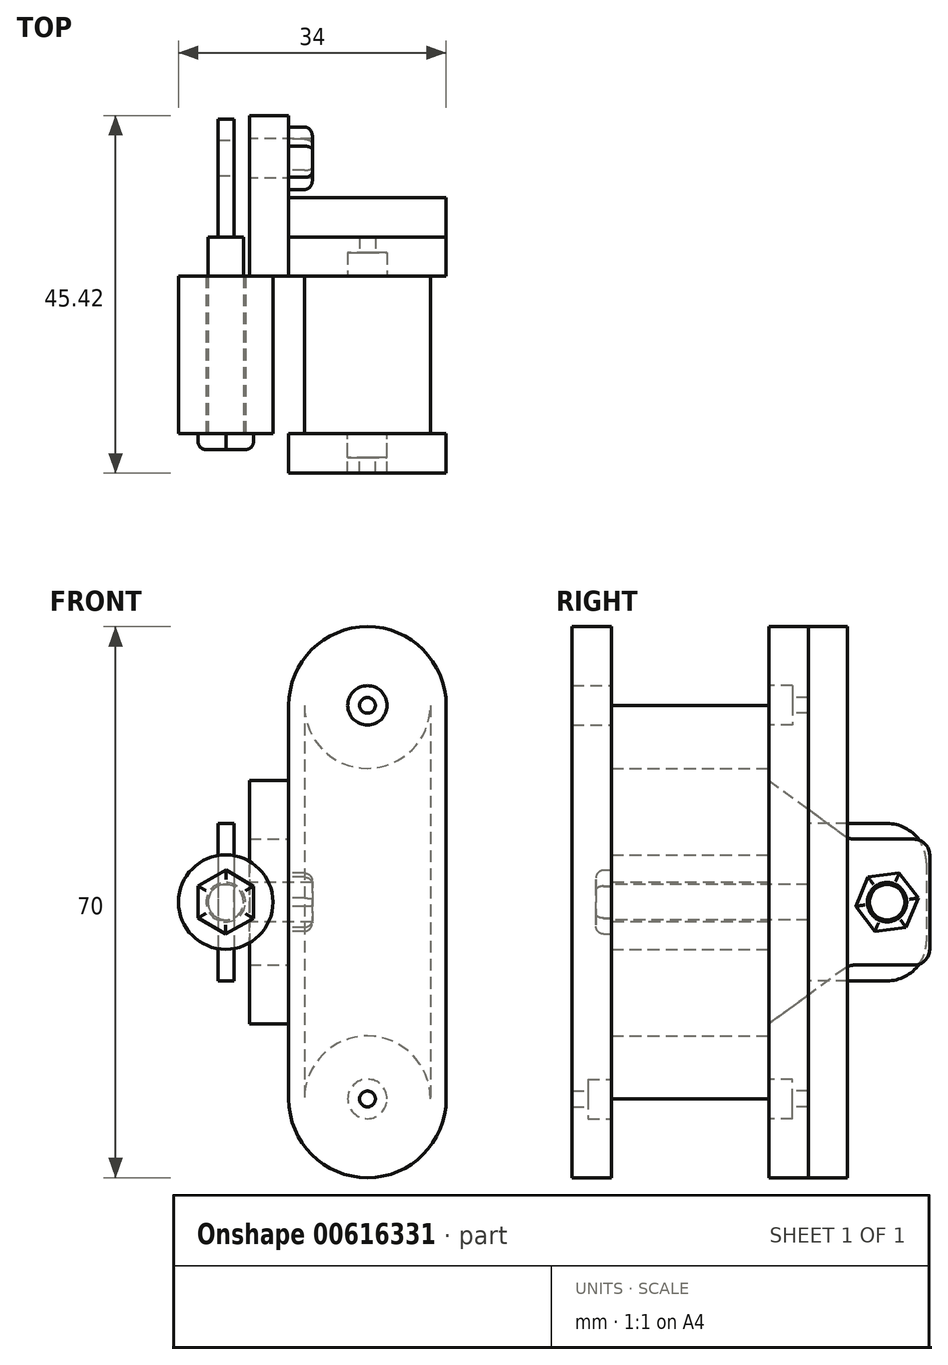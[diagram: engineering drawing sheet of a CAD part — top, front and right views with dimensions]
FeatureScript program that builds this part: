
annotation { "Feature Type Name" : "Feature", "Feature Type Description" : "" }
export const myFeature = defineFeature(function(context is Context, id is Id, definition is map)
    precondition{}
    {
        {
            var Q0;
            Q0=qCreatedBy(makeId("Right.planeOp"),FACE);
            var sketch = newSketch(context, id + "F0", { "sketchPlane" : qUnion([Q0])});
            skLineSegment(sketch, "E0.bottom", {"start": v(10, 0) * mm, "end": v(-10, 0) * mm});
            skLineSegment(sketch, "E0.top", {"start": v(10, -25) * mm, "end": v(-10, -25) * mm});
            skLineSegment(sketch, "E0.left", {"start": v(10, 0) * mm, "end": v(10, -25) * mm});
            skLineSegment(sketch, "E0.right", {"start": v(-10, 0) * mm, "end": v(-10, -25) * mm});
            skPoint(sketch, "E0.middle", {"position": v(0, -12.5) * mm});
            skSolve(sketch);
        }
        {
            var Q0;
            Q0 = qSketchRegion(id + "F0", true);
            extrude(context, id + "F1", {"entities" : qUnion([Q0]), "depth" : 16 * mm, "offsetDistance" : 25 * mm});
        }
        {
            var Q0;
            Q0=makeQuery(id+"F1.opExtrude","SWEPT_FACE",FACE,{"disambiguationData":[OSD([sQuery(id+"F0.wireOp",EDGE,"E0.left")])]});
            var sketch = newSketch(context, id + "F2", { "sketchPlane" : qUnion([Q0])});
            skArc(sketch, "E1", {"start": v(0, -25) * mm, "mid": v(-8, -17) * mm, "end": v(-16, -25) * mm});
            skLineSegment(sketch, "E2", {"start": v(-16, -25) * mm, "end": v(0, -25) * mm});
            skSolve(sketch);
        }
        {
            var Q0;
            Q0 = qSketchRegion(id + "F2", true);
            extrude(context, id + "F3", {"entities" : qUnion([Q0]), "operationType" : NewBodyOperationType.REMOVE, "endBound" : BoundingType.THROUGH_ALL, "oppositeDirection" : true, "depth" : 25 * mm, "offsetDistance" : 25 * mm});
        }
        {
            var Q0;
            Q0=makeQuery(id+"F1.opExtrude","SWEPT_FACE",FACE,{"disambiguationData":[OSD([sQuery(id+"F0.wireOp",EDGE,"E0.left")])]});
            var sketch = newSketch(context, id + "F4", { "sketchPlane" : qUnion([Q0])});
            skArc(sketch, "E3", {"start": v(-18, -25) * mm, "mid": v(-8, -35) * mm, "end": v(2, -25) * mm});
            skLineSegment(sketch, "E4", {"start": v(-18, -25) * mm, "end": v(-18, 0) * mm});
            skLineSegment(sketch, "E5", {"start": v(-18, 0) * mm, "end": v(2, 0) * mm});
            skLineSegment(sketch, "E6", {"start": v(2, 0) * mm, "end": v(2, -25) * mm});
            skSolve(sketch);
        }
        {
            var Q0;
            Q0 = qSketchRegion(id + "F4", true);
            extrude(context, id + "F5", {"entities" : qUnion([Q0]), "operationType" : NewBodyOperationType.ADD, "depth" : 5 * mm, "offsetDistance" : 25 * mm});
        }
        {
            var Q0;
            Q0=makeQuery(id+"F5.opExtrude","CAP_FACE",FACE,{"disambiguationData":[OSD([sQuery(id+"F4.wireOp",EDGE,"E3"),sQuery(id+"F4.wireOp",EDGE,"E4"),sQuery(id+"F4.wireOp",EDGE,"E5"),sQuery(id+"F4.wireOp",EDGE,"E6")])],"isStart":true});
            var sketch = newSketch(context, id + "F6", { "sketchPlane" : qUnion([Q0])});
            skCircle(sketch, "E7", {"center": v(8, -25) * mm, "radius": 2.5 * mm});
            skSolve(sketch);
        }
        {
            var Q0;
            Q0 = qSketchRegion(id + "F6", true);
            extrude(context, id + "F7", {"entities" : qUnion([Q0]), "operationType" : NewBodyOperationType.REMOVE, "oppositeDirection" : true, "depth" : 3 * mm, "offsetDistance" : 25 * mm});
        }
        {
            var Q0;
            Q0=makeQuery(id+"F7.boolean.opBoolean","COPY",FACE,{"derivedFrom":makeQuery(id+"F7.opExtrude","CAP_FACE",FACE,{"disambiguationData":[OSD([sQuery(id+"F6.wireOp",EDGE,"E7")])],"isStart":false})});
            var sketch = newSketch(context, id + "F8", { "sketchPlane" : qUnion([Q0])});
            skCircle(sketch, "E8", {"center": v(8, -25) * mm, "radius": 1 * mm});
            skSolve(sketch);
        }
        {
            var Q0;
            Q0 = qSketchRegion(id + "F8", true);
            extrude(context, id + "F9", {"entities" : qUnion([Q0]), "operationType" : NewBodyOperationType.REMOVE, "endBound" : BoundingType.THROUGH_ALL, "oppositeDirection" : true, "depth" : 25 * mm, "offsetDistance" : 25 * mm});
        }
        {
            var Q0;
            Q0=makeQuery(id+"F1.opExtrude","SWEPT_BODY",BODY,{"disambiguationData":[OSD([sQuery(id+"F0.wireOp",EDGE,"E0.bottom"),sQuery(id+"F0.wireOp",EDGE,"E0.top"),sQuery(id+"F0.wireOp",EDGE,"E0.left"),sQuery(id+"F0.wireOp",EDGE,"E0.right")])]});
            var Q1;
            Q1=qCreatedBy(makeId("Top.planeOp"),FACE);
            mirror(context, id + "F10", {"operationType" : NewBodyOperationType.ADD, "entities" : qUnion([Q0]), "mirrorPlane" : qUnion([Q1])});
        }
        {
            var Q0;
            {var subQ0=makeQuery(id+"F1.opExtrude","SWEPT_FACE",FACE,{"disambiguationData":[OSD([sQuery(id+"F0.wireOp",EDGE,"E0.right")])]});Q0=makeQuery(id+"F10.boolean.opBoolean","MERGE",FACE,{"derivedFrom":[subQ0,makeQuery(id+"F10.opPattern","COPY",FACE,{"derivedFrom":subQ0,"instanceName":"1"})]});}
            var sketch = newSketch(context, id + "F11", { "sketchPlane" : qUnion([Q0])});
            skLineSegment(sketch, "E9", {"start": v(-2, -25) * mm, "end": v(-2, 25) * mm});
            skLineSegment(sketch, "E10", {"start": v(18, 25) * mm, "end": v(18, -25) * mm});
            skArc(sketch, "E11", {"start": v(-2, -25) * mm, "mid": v(8, -35) * mm, "end": v(18, -25) * mm});
            skArc(sketch, "E12", {"start": v(18, 25) * mm, "mid": v(8, 35) * mm, "end": v(-2, 25) * mm});
            skCircle(sketch, "E13", {"center": v(8, 25) * mm, "radius": 2.5 * mm});
            skSolve(sketch);
        }
        {
            var Q0;
            {var subQ0=sQuery(id+"F0.wireOp",EDGE,"E0.right");var subQ1=makeQuery(id+"F3.boolean.opBoolean","INTERSECT",EDGE,{"derivedFrom":[makeQuery(id+"F1.opExtrude","SWEPT_FACE",FACE,{"disambiguationData":[OSD([subQ0])]}),makeQuery(id+"F3.opExtrude","SWEPT_FACE",FACE,{"disambiguationData":[OSD([sQuery(id+"F2.wireOp",EDGE,"E1")])]})]});Q0=makeQuery(id+"F11.imprint","IMPRINT",FACE,{"disambiguationData":[TD([[makeQuery(id+"F11.imprint","IMPRINT",EDGE,{"derivedFrom":subQ1}),1.0]])]});}
            var Q1;
            Q1=makeQuery(id+"F11.imprint","IMPRINT",FACE,{"disambiguationData":[TD([[makeQuery(id+"F11.imprint","IMPRINT",EDGE,{"derivedFrom":sQuery(id+"F11.wireOp",EDGE,"E9")}),-1.0]])]});
            extrude(context, id + "F12", {"entities" : qUnion([Q0, Q1]), "depth" : 5 * mm, "offsetDistance" : 25 * mm});
        }
        {
            var Q0;
            Q0=makeQuery(id+"F12.opExtrude","CAP_FACE",FACE,{"disambiguationData":[OSD([sQuery(id+"F11.wireOp",EDGE,"E9"),sQuery(id+"F11.wireOp",EDGE,"E10"),sQuery(id+"F11.wireOp",EDGE,"E11"),sQuery(id+"F11.wireOp",EDGE,"E12"),sQuery(id+"F11.wireOp",EDGE,"E13")])],"isStart":true});
            var sketch = newSketch(context, id + "F13", { "sketchPlane" : qUnion([Q0])});
            skCircle(sketch, "E14", {"center": v(-8, -25) * mm, "radius": 2.5 * mm});
            skSolve(sketch);
        }
        {
            var Q0;
            Q0 = qSketchRegion(id + "F13", true);
            extrude(context, id + "F14", {"entities" : qUnion([Q0]), "operationType" : NewBodyOperationType.REMOVE, "oppositeDirection" : true, "depth" : 3 * mm, "offsetDistance" : 25 * mm});
        }
        {
            var Q0;
            Q0=makeQuery(id+"F14.boolean.opBoolean","COPY",FACE,{"derivedFrom":makeQuery(id+"F14.opExtrude","CAP_FACE",FACE,{"disambiguationData":[OSD([sQuery(id+"F13.wireOp",EDGE,"E14")])],"isStart":false})});
            var sketch = newSketch(context, id + "F15", { "sketchPlane" : qUnion([Q0])});
            skCircle(sketch, "E15", {"center": v(-8, -25) * mm, "radius": 1 * mm});
            skSolve(sketch);
        }
        {
            var Q0;
            Q0 = qSketchRegion(id + "F15", true);
            extrude(context, id + "F16", {"entities" : qUnion([Q0]), "operationType" : NewBodyOperationType.REMOVE, "endBound" : BoundingType.THROUGH_ALL, "oppositeDirection" : true, "depth" : 25 * mm, "offsetDistance" : 25 * mm});
        }
        {
            var Q0;
            {var subQ0=makeQuery(id+"F5.opExtrude","SWEPT_FACE",FACE,{"disambiguationData":[OSD([sQuery(id+"F4.wireOp",EDGE,"E6")])]});Q0=makeQuery(id+"F10.boolean.opBoolean","MERGE",FACE,{"derivedFrom":[subQ0,makeQuery(id+"F10.opPattern","COPY",FACE,{"derivedFrom":subQ0,"instanceName":"1"})]});}
            var sketch = newSketch(context, id + "F17", { "sketchPlane" : qUnion([Q0])});
            skLineSegment(sketch, "E16.bottom", {"start": v(-20.86, -8) * mm, "end": v(-28.42, -8) * mm});
            skLineSegment(sketch, "E16.top", {"start": v(-20.86, 8) * mm, "end": v(-28.42, 8) * mm});
            skLineSegment(sketch, "E16.left", {"start": v(-10, -8) * mm, "end": v(-10, 8) * mm});
            skLineSegment(sketch, "E16.right", {"start": v(-30.42, -6) * mm, "end": v(-30.42, 6) * mm});
            skLineSegment(sketch, "E17", {"start": v(-19.68, -8.39) * mm, "end": v(-10, -15.48) * mm});
            skLineSegment(sketch, "E18", {"start": v(-10, -15.48) * mm, "end": v(-10, 15.48) * mm});
            skLineSegment(sketch, "E19", {"start": v(-10, 15.48) * mm, "end": v(-19.68, 8.39) * mm});
            skPoint(sketch, "E20.visualSharp", {"position": v(-30.42, 8) * mm});
            skArc(sketch, "E20.filletArc", {"start": v(-28.42, 8) * mm, "mid": v(-29.83, 7.41) * mm, "end": v(-30.42, 6) * mm});
            skPoint(sketch, "E21.visualSharp", {"position": v(-30.42, -8) * mm});
            skArc(sketch, "E21.filletArc", {"start": v(-30.42, -6) * mm, "mid": v(-29.83, -7.41) * mm, "end": v(-28.42, -8) * mm});
            skPoint(sketch, "E22.visualSharp", {"position": v(-20.2, -8) * mm});
            skArc(sketch, "E22.filletArc", {"start": v(-19.68, -8.39) * mm, "mid": v(-20.24, -8.1) * mm, "end": v(-20.86, -8) * mm});
            skPoint(sketch, "E23.visualSharp", {"position": v(-20.2, 8) * mm});
            skArc(sketch, "E23.filletArc", {"start": v(-20.86, 8) * mm, "mid": v(-20.24, 8.1) * mm, "end": v(-19.68, 8.39) * mm});
            skSolve(sketch);
        }
        {
            var Q0;
            Q0 = qSketchRegion(id + "F17", true);
            extrude(context, id + "F18", {"entities" : qUnion([Q0]), "operationType" : NewBodyOperationType.ADD, "depth" : 5 * mm, "offsetDistance" : 25 * mm});
        }
        {
            var Q0;
            Q0=makeQuery(id+"F18.opExtrude","CAP_FACE",FACE,{"disambiguationData":[OSD([sQuery(id+"F17.wireOp",EDGE,"E16.bottom"),sQuery(id+"F17.wireOp",EDGE,"E16.top"),sQuery(id+"F17.wireOp",EDGE,"E16.right"),sQuery(id+"F17.wireOp",EDGE,"E17"),sQuery(id+"F17.wireOp",EDGE,"E18"),sQuery(id+"F17.wireOp",EDGE,"E19"),sQuery(id+"F17.wireOp",EDGE,"E20.filletArc"),sQuery(id+"F17.wireOp",EDGE,"E21.filletArc"),sQuery(id+"F17.wireOp",EDGE,"E22.filletArc"),sQuery(id+"F17.wireOp",EDGE,"E23.filletArc")])],"isStart":false});
            var sketch = newSketch(context, id + "F19", { "sketchPlane" : qUnion([Q0])});
            skCircle(sketch, "E24", {"center": v(-25, 0) * mm, "radius": 2.5 * mm});
            skPoint(sketch, "E24.centerSnap0", {"position": v(-10, 0) * mm});
            skSolve(sketch);
        }
        {
            var Q0;
            Q0 = qSketchRegion(id + "F19", true);
            extrude(context, id + "F20", {"entities" : qUnion([Q0]), "operationType" : NewBodyOperationType.REMOVE, "endBound" : BoundingType.THROUGH_ALL, "oppositeDirection" : true, "depth" : 25 * mm, "offsetDistance" : 25 * mm});
        }
        {
            var Q0;
            Q0=makeQuery(id+"F18.opExtrude","CAP_FACE",FACE,{"disambiguationData":[OSD([sQuery(id+"F17.wireOp",EDGE,"E16.bottom"),sQuery(id+"F17.wireOp",EDGE,"E16.top"),sQuery(id+"F17.wireOp",EDGE,"E16.right"),sQuery(id+"F17.wireOp",EDGE,"E17"),sQuery(id+"F17.wireOp",EDGE,"E18"),sQuery(id+"F17.wireOp",EDGE,"E19"),sQuery(id+"F17.wireOp",EDGE,"E20.filletArc"),sQuery(id+"F17.wireOp",EDGE,"E21.filletArc"),sQuery(id+"F17.wireOp",EDGE,"E22.filletArc"),sQuery(id+"F17.wireOp",EDGE,"E23.filletArc")])],"isStart":true});
            var sketch = newSketch(context, id + "F21", { "sketchPlane" : qUnion([Q0])});
            skCircle(sketch, "E25.cCircle", {"center": v(25, 0) * mm, "radius": 4 * mm, "construction": true});
            skLineSegment(sketch, "E25.0", {"start": v(22.57, 3.18) * mm, "end": v(26.54, 3.7) * mm});
            skLineSegment(sketch, "E25.1", {"start": v(26.54, 3.7) * mm, "end": v(28.97, 0.51) * mm});
            skLineSegment(sketch, "E25.2", {"start": v(28.97, 0.51) * mm, "end": v(27.43, -3.18) * mm});
            skLineSegment(sketch, "E25.3", {"start": v(27.43, -3.18) * mm, "end": v(23.46, -3.7) * mm});
            skLineSegment(sketch, "E25.4", {"start": v(23.46, -3.7) * mm, "end": v(21.03, -0.51) * mm});
            skLineSegment(sketch, "E25.5", {"start": v(21.03, -0.51) * mm, "end": v(22.57, 3.18) * mm});
            skCircle(sketch, "E26", {"center": v(25, 0) * mm, "radius": 2.5 * mm});
            skSolve(sketch);
        }
        {
            var Q0;
            Q0 = qSketchRegion(id + "F21", true);
            extrude(context, id + "F22", {"entities" : qUnion([Q0]), "operationType" : NewBodyOperationType.ADD, "depth" : 3 * mm, "offsetDistance" : 25 * mm});
        }
        {
            var Q0;
            Q0=makeQuery(id+"F22.opExtrude","CAP_EDGE",EDGE,{"disambiguationData":[OSD([sQuery(id+"F21.wireOp",EDGE,"E25.0")])],"isStart":false});
            var Q1;
            Q1=makeQuery(id+"F22.opExtrude","CAP_EDGE",EDGE,{"disambiguationData":[OSD([sQuery(id+"F21.wireOp",EDGE,"E25.5")])],"isStart":false});
            var Q2;
            Q2=makeQuery(id+"F22.opExtrude","CAP_EDGE",EDGE,{"disambiguationData":[OSD([sQuery(id+"F21.wireOp",EDGE,"E25.4")])],"isStart":false});
            var Q3;
            Q3=makeQuery(id+"F22.opExtrude","CAP_EDGE",EDGE,{"disambiguationData":[OSD([sQuery(id+"F21.wireOp",EDGE,"E25.3")])],"isStart":false});
            var Q4;
            Q4=makeQuery(id+"F22.opExtrude","CAP_EDGE",EDGE,{"disambiguationData":[OSD([sQuery(id+"F21.wireOp",EDGE,"E25.2")])],"isStart":false});
            var Q5;
            Q5=makeQuery(id+"F22.opExtrude","CAP_EDGE",EDGE,{"disambiguationData":[OSD([sQuery(id+"F21.wireOp",EDGE,"E25.1")])],"isStart":false});
            fillet(context, id + "F23", {"entities" : qUnion([Q0, Q1, Q2, Q3, Q4, Q5]), "radius" : 1 * mm, "tangentPropagation" : true, "allowEdgeOverflow" : false});
        }
        {
            var Q0;
            {var subQ0=makeQuery(id+"F5.opExtrude","CAP_FACE",FACE,{"disambiguationData":[OSD([sQuery(id+"F4.wireOp",EDGE,"E3"),sQuery(id+"F4.wireOp",EDGE,"E4"),sQuery(id+"F4.wireOp",EDGE,"E5"),sQuery(id+"F4.wireOp",EDGE,"E6")])],"isStart":false});Q0=makeQuery(id+"F10.boolean.opBoolean","MERGE",FACE,{"derivedFrom":[subQ0,makeQuery(id+"F10.opPattern","COPY",FACE,{"derivedFrom":subQ0,"instanceName":"1"})]});}
            var sketch = newSketch(context, id + "F24", { "sketchPlane" : qUnion([Q0])});
            skLineSegment(sketch, "E27", {"start": v(-18, -25) * mm, "end": v(-18, 25) * mm});
            skLineSegment(sketch, "E28", {"start": v(2, -25) * mm, "end": v(2, 25) * mm});
            skArc(sketch, "E29", {"start": v(2, 25) * mm, "mid": v(-8, 35) * mm, "end": v(-18, 25) * mm});
            skArc(sketch, "E30", {"start": v(-18, -25) * mm, "mid": v(-8, -35) * mm, "end": v(2, -25) * mm});
            skSolve(sketch);
        }
        {
            var Q0;
            Q0 = qSketchRegion(id + "F24", true);
            extrude(context, id + "F25", {"entities" : qUnion([Q0]), "depth" : 5 * mm, "offsetDistance" : 25 * mm});
        }
        {
            var Q0;
            {var subQ0=makeQuery(id+"F5.opExtrude","CAP_FACE",FACE,{"disambiguationData":[OSD([sQuery(id+"F4.wireOp",EDGE,"E3"),sQuery(id+"F4.wireOp",EDGE,"E4"),sQuery(id+"F4.wireOp",EDGE,"E5"),sQuery(id+"F4.wireOp",EDGE,"E6")])],"isStart":true});Q0=makeQuery(id+"F18.boolean.opBoolean","MERGE",FACE,{"derivedFrom":[makeQuery(id+"F10.boolean.opBoolean","MERGE",FACE,{"derivedFrom":[subQ0,makeQuery(id+"F10.opPattern","COPY",FACE,{"derivedFrom":subQ0,"instanceName":"1"})]}),makeQuery(id+"F18.opExtrude","SWEPT_FACE",FACE,{"disambiguationData":[OSD([sQuery(id+"F17.wireOp",EDGE,"E18")])]})]});}
            var sketch = newSketch(context, id + "F26", { "sketchPlane" : qUnion([Q0])});
            skCircle(sketch, "E31", {"center": v(-10, 0) * mm, "radius": 6 * mm});
            skPoint(sketch, "E31.centerSnap0", {"position": v(-7, 0) * mm});
            skSolve(sketch);
        }
        {
            var Q0;
            Q0 = qSketchRegion(id + "F26", true);
            extrude(context, id + "F27", {"entities" : qUnion([Q0]), "depth" : 20 * mm, "offsetDistance" : 25 * mm});
        }
        {
            var Q0;
            Q0=makeQuery(id+"F27.opExtrude","CAP_FACE",FACE,{"disambiguationData":[OSD([sQuery(id+"F26.wireOp",EDGE,"E31")])],"isStart":false});
            var sketch = newSketch(context, id + "F28", { "sketchPlane" : qUnion([Q0])});
            skCircle(sketch, "E32", {"center": v(-10, 0) * mm, "radius": 2.5 * mm});
            skSolve(sketch);
        }
        {
            var Q0;
            Q0 = qSketchRegion(id + "F28", true);
            extrude(context, id + "F29", {"entities" : qUnion([Q0]), "operationType" : NewBodyOperationType.REMOVE, "endBound" : BoundingType.THROUGH_ALL, "oppositeDirection" : true, "depth" : 25 * mm, "offsetDistance" : 25 * mm});
        }
        {
            var Q0;
            Q0=makeQuery(id+"F27.opExtrude","CAP_FACE",FACE,{"disambiguationData":[OSD([sQuery(id+"F26.wireOp",EDGE,"E31")])],"isStart":false});
            var sketch = newSketch(context, id + "F30", { "sketchPlane" : qUnion([Q0])});
            skCircle(sketch, "E33.cCircle", {"center": v(-10, 0) * mm, "radius": 4.06 * mm, "construction": true});
            skLineSegment(sketch, "E33.0", {"start": v(-6.48, 2.02) * mm, "end": v(-6.49, -2.04) * mm});
            skLineSegment(sketch, "E33.1", {"start": v(-6.49, -2.04) * mm, "end": v(-10.01, -4.06) * mm});
            skLineSegment(sketch, "E33.2", {"start": v(-10.01, -4.06) * mm, "end": v(-13.52, -2.02) * mm});
            skLineSegment(sketch, "E33.3", {"start": v(-13.52, -2.02) * mm, "end": v(-13.51, 2.04) * mm});
            skLineSegment(sketch, "E33.4", {"start": v(-13.51, 2.04) * mm, "end": v(-9.99, 4.06) * mm});
            skLineSegment(sketch, "E33.5", {"start": v(-9.99, 4.06) * mm, "end": v(-6.48, 2.02) * mm});
            skSolve(sketch);
        }
        {
            var Q0;
            Q0 = qSketchRegion(id + "F30", true);
            extrude(context, id + "F31", {"entities" : qUnion([Q0]), "depth" : 2 * mm, "offsetDistance" : 25 * mm});
        }
        {
            var Q0;
            Q0=makeQuery(id+"F31.opExtrude","CAP_EDGE",EDGE,{"disambiguationData":[OSD([sQuery(id+"F30.wireOp",EDGE,"E33.4")])],"isStart":false});
            var Q1;
            Q1=makeQuery(id+"F31.opExtrude","CAP_EDGE",EDGE,{"disambiguationData":[OSD([sQuery(id+"F30.wireOp",EDGE,"E33.3")])],"isStart":false});
            var Q2;
            Q2=makeQuery(id+"F31.opExtrude","CAP_EDGE",EDGE,{"disambiguationData":[OSD([sQuery(id+"F30.wireOp",EDGE,"E33.2")])],"isStart":false});
            var Q3;
            Q3=makeQuery(id+"F31.opExtrude","CAP_EDGE",EDGE,{"disambiguationData":[OSD([sQuery(id+"F30.wireOp",EDGE,"E33.1")])],"isStart":false});
            var Q4;
            Q4=makeQuery(id+"F31.opExtrude","CAP_EDGE",EDGE,{"disambiguationData":[OSD([sQuery(id+"F30.wireOp",EDGE,"E33.0")])],"isStart":false});
            var Q5;
            Q5=makeQuery(id+"F31.opExtrude","CAP_EDGE",EDGE,{"disambiguationData":[OSD([sQuery(id+"F30.wireOp",EDGE,"E33.5")])],"isStart":false});
            fillet(context, id + "F32", {"entities" : qUnion([Q0, Q1, Q2, Q3, Q4, Q5]), "radius" : 1 * mm, "tangentPropagation" : true, "allowEdgeOverflow" : false});
        }
        {
            var Q0;
            Q0=makeQuery(id+"F31.opExtrude","CAP_FACE",FACE,{"disambiguationData":[OSD([sQuery(id+"F30.wireOp",EDGE,"E33.0"),sQuery(id+"F30.wireOp",EDGE,"E33.1"),sQuery(id+"F30.wireOp",EDGE,"E33.2"),sQuery(id+"F30.wireOp",EDGE,"E33.3"),sQuery(id+"F30.wireOp",EDGE,"E33.4"),sQuery(id+"F30.wireOp",EDGE,"E33.5")])],"isStart":true});
            var sketch = newSketch(context, id + "F33", { "sketchPlane" : qUnion([Q0])});
            skCircle(sketch, "E34", {"center": v(10, 0) * mm, "radius": 2.25 * mm});
            skSolve(sketch);
        }
        {
            var Q0;
            Q0 = qSketchRegion(id + "F33", true);
            extrude(context, id + "F34", {"entities" : qUnion([Q0]), "operationType" : NewBodyOperationType.ADD, "depth" : 25 * mm, "offsetDistance" : 25 * mm});
        }
        {
            var Q0;
            Q0=makeQuery(id+"F34.opExtrude","CAP_FACE",FACE,{"disambiguationData":[OSD([sQuery(id+"F33.wireOp",EDGE,"E34")])],"isStart":false});
            var sketch = newSketch(context, id + "F35", { "sketchPlane" : qUnion([Q0])});
            skLineSegment(sketch, "E35.bottom", {"start": v(8.96, 10) * mm, "end": v(10.96, 10) * mm});
            skLineSegment(sketch, "E35.top", {"start": v(8.96, -10) * mm, "end": v(10.96, -10) * mm});
            skLineSegment(sketch, "E35.left", {"start": v(8.96, 10) * mm, "end": v(8.96, -10) * mm});
            skLineSegment(sketch, "E35.right", {"start": v(10.96, 10) * mm, "end": v(10.96, -10) * mm});
            skSolve(sketch);
        }
        {
            var Q0;
            Q0 = qSketchRegion(id + "F35", true);
            extrude(context, id + "F36", {"entities" : qUnion([Q0]), "operationType" : NewBodyOperationType.ADD, "depth" : 15 * mm, "offsetDistance" : 25 * mm});
        }
        {
            var Q0;
            Q0=makeQuery(id+"F36.opExtrude","CAP_EDGE",EDGE,{"disambiguationData":[OSD([sQuery(id+"F35.wireOp",EDGE,"E35.bottom")])],"isStart":false});
            var Q1;
            Q1=makeQuery(id+"F36.opExtrude","CAP_EDGE",EDGE,{"disambiguationData":[OSD([sQuery(id+"F35.wireOp",EDGE,"E35.top")])],"isStart":false});
            fillet(context, id + "F37", {"entities" : qUnion([Q0, Q1]), "radius" : 5 * mm, "tangentPropagation" : true, "allowEdgeOverflow" : false});
        }
        {
            var Q0;
            Q0=makeQuery(id+"F36.opExtrude","SWEPT_FACE",FACE,{"disambiguationData":[OSD([sQuery(id+"F35.wireOp",EDGE,"E35.left")])]});
            var sketch = newSketch(context, id + "F38", { "sketchPlane" : qUnion([Q0])});
            skCircle(sketch, "E36", {"center": v(25.02, 0) * mm, "radius": 2.25 * mm});
            skSolve(sketch);
        }
        {
            var Q0;
            Q0 = qSketchRegion(id + "F38", true);
            extrude(context, id + "F39", {"entities" : qUnion([Q0]), "operationType" : NewBodyOperationType.REMOVE, "endBound" : BoundingType.THROUGH_ALL, "oppositeDirection" : true, "depth" : 25 * mm, "offsetDistance" : 25 * mm});
        }
    });
